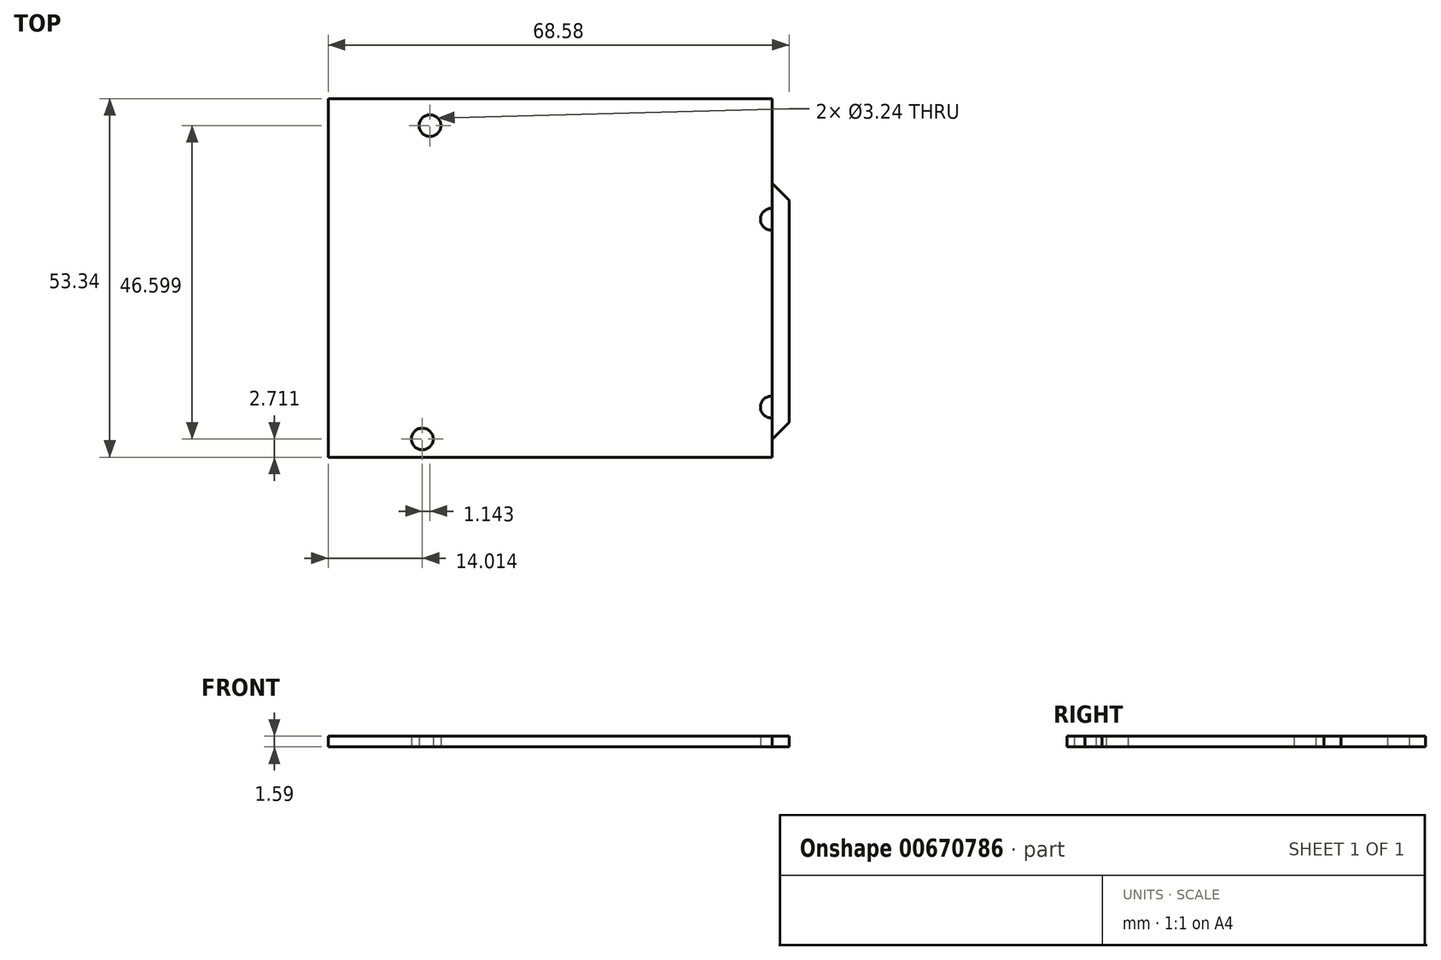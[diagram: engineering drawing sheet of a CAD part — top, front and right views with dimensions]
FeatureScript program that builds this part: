
annotation { "Feature Type Name" : "Feature", "Feature Type Description" : "" }
export const myFeature = defineFeature(function(context is Context, id is Id, definition is map)
    precondition{}
    {
        {
            var Q0;
            Q0=qCreatedBy(makeId("Top.planeOp"),FACE);
            var sketch = newSketch(context, id + "F0", { "sketchPlane" : qUnion([Q0])});
            skLineSegment(sketch, "E0", {"start": v(-33.02, 26.67) * mm, "end": v(33.02, 26.67) * mm});
            skLineSegment(sketch, "E1", {"start": v(33.02, 26.67) * mm, "end": v(33.02, -26.67) * mm});
            skLineSegment(sketch, "E2", {"start": v(33.02, -26.67) * mm, "end": v(-33.02, -26.67) * mm});
            skLineSegment(sketch, "E3", {"start": v(-33.02, -26.67) * mm, "end": v(-33.02, 26.67) * mm});
            skLineSegment(sketch, "E4", {"start": v(0, 0) * mm, "end": v(-33.02, 0) * mm, "construction": true});
            skPoint(sketch, "E4.endSnap0", {"position": v(-33.02, 0) * mm});
            skLineSegment(sketch, "E5", {"start": v(0, 0) * mm, "end": v(0, 26.67) * mm, "construction": true});
            skLineSegment(sketch, "E6", {"start": v(33.02, 14.1) * mm, "end": v(35.56, 11.56) * mm});
            skLineSegment(sketch, "E7", {"start": v(35.56, 11.56) * mm, "end": v(35.56, -21.46) * mm});
            skLineSegment(sketch, "E8", {"start": v(35.56, -21.46) * mm, "end": v(33.02, -24) * mm});
            skSolve(sketch);
        }
        {
            var Q0;
            {var subQ4=sQuery(id+"F0.wireOp",EDGE,"E0");Q0=makeQuery(id+"F0.imprint","IMPRINT",FACE,{"disambiguationData":[TD([[makeQuery(id+"F0.imprint","IMPRINT",EDGE,{"derivedFrom":subQ4}),-1.0]])]});}
            var sketch = newSketch(context, id + "F1", { "sketchPlane" : qUnion([Q0])});
            skCircle(sketch, "E9", {"center": v(-17.86, 22.64) * mm, "radius": 1.62 * mm});
            skCircle(sketch, "E10", {"center": v(32.92, 8.72) * mm, "radius": 1.62 * mm});
            skCircle(sketch, "E11", {"center": v(32.93, -19.2) * mm, "radius": 1.62 * mm});
            skCircle(sketch, "E12", {"center": v(-19, -23.96) * mm, "radius": 1.62 * mm});
            skSolve(sketch);
        }
        {
            var Q0;
            Q0=makeQuery(id+"F1.imprint","IMPRINT",FACE,{"disambiguationData":[TD([[makeQuery(id+"F1.imprint","IMPRINT",EDGE,{"derivedFrom":sQuery(id+"F1.wireOp",EDGE,"E9")}),-1.0]])]});
            var Q1;
            {var subQ0=sQuery(id+"F0.wireOp",EDGE,"E6");Q1=makeQuery(id+"F0.imprint","IMPRINT",FACE,{"disambiguationData":[TD([[makeQuery(id+"F0.imprint","IMPRINT",EDGE,{"derivedFrom":subQ0}),-1.0]])]});}
            extrude(context, id + "F2", {"entities" : qUnion([Q0, Q1]), "depth" : 1.59 * mm, "offsetDistance" : 25 * mm});
        }
    });
